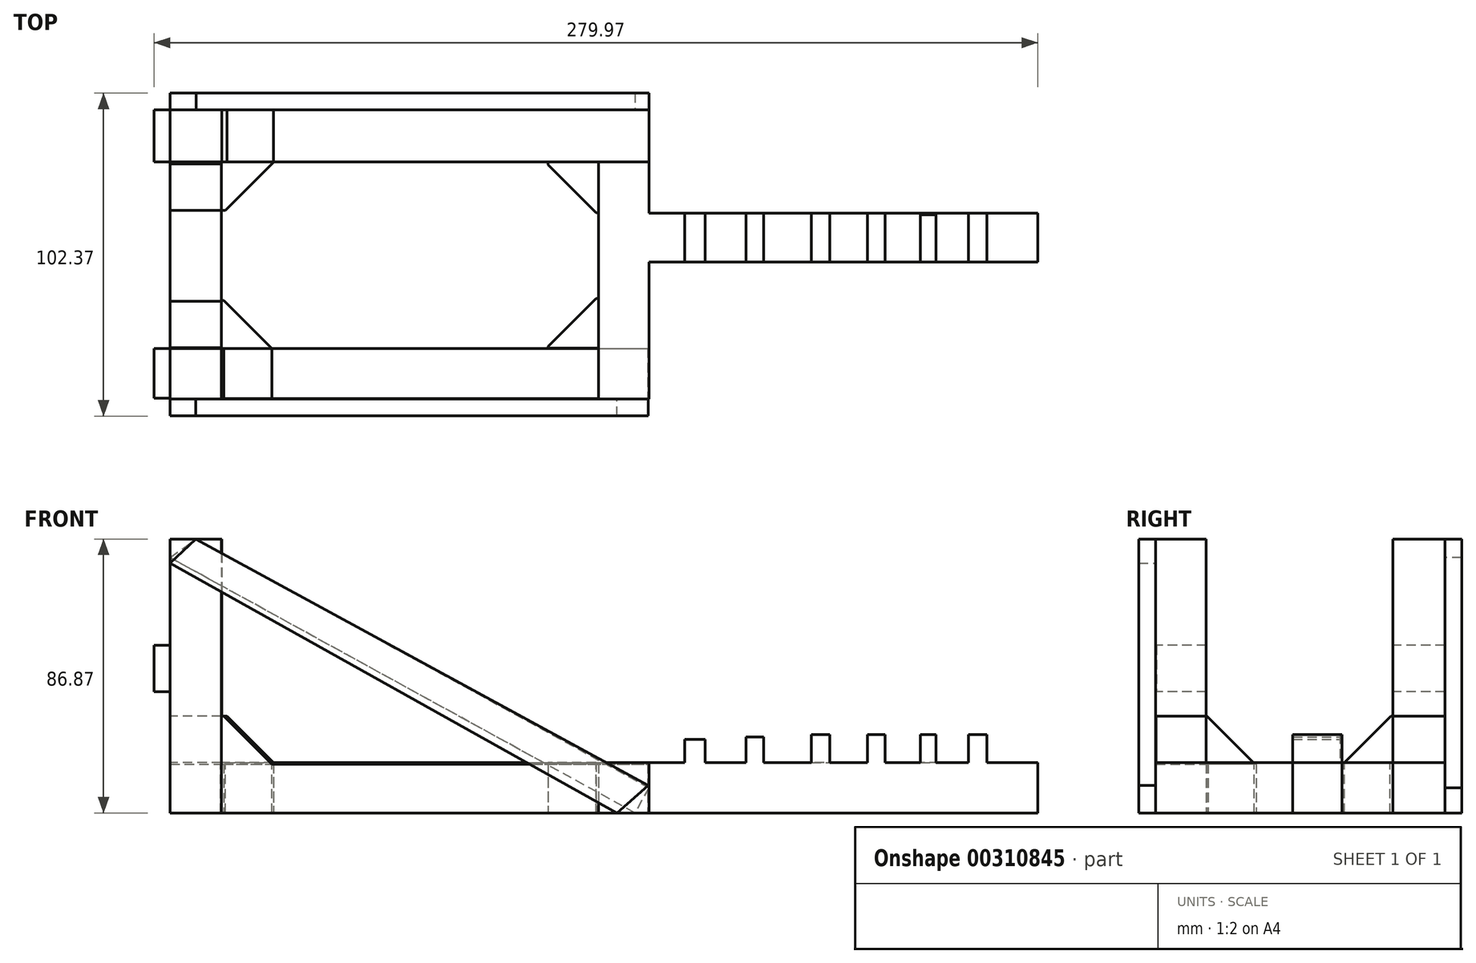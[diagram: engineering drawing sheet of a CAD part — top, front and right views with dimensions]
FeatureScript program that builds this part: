
annotation { "Feature Type Name" : "Feature", "Feature Type Description" : "" }
export const myFeature = defineFeature(function(context is Context, id is Id, definition is map)
    precondition{}
    {
        {
            var Q0;
            Q0=qCreatedBy(makeId("Top.planeOp"),FACE);
            var sketch = newSketch(context, id + "F0", { "sketchPlane" : qUnion([Q0])});
            skLineSegment(sketch, "E0.bottom", {"start": v(-76.1, 76.76) * mm, "end": v(75.59, 76.76) * mm});
            skLineSegment(sketch, "E0.top", {"start": v(-76.1, -76.47) * mm, "end": v(75.59, -76.47) * mm});
            skLineSegment(sketch, "E0.left", {"start": v(-76.1, 76.76) * mm, "end": v(-76.1, -76.47) * mm});
            skLineSegment(sketch, "E0.right", {"start": v(75.59, 76.76) * mm, "end": v(75.59, -76.47) * mm});
            skSolve(sketch);
        }
        {
            var Q0;
            Q0=makeQuery(id+"F0.imprint","IMPRINT",FACE,{"disambiguationData":[TD([[makeQuery(id+"F0.imprint","IMPRINT",EDGE,{"derivedFrom":sQuery(id+"F0.wireOp",EDGE,"E0.bottom")}),-1.0]])]});
            var sketch = newSketch(context, id + "F1", { "sketchPlane" : qUnion([Q0])});
            skLineSegment(sketch, "E1.bottom", {"start": v(-76.15, -35.2) * mm, "end": v(75.3, -35.2) * mm});
            skLineSegment(sketch, "E1.top", {"start": v(-76.15, -51.18) * mm, "end": v(75.3, -51.18) * mm});
            skLineSegment(sketch, "E1.left", {"start": v(-76.15, -35.2) * mm, "end": v(-76.15, -51.18) * mm});
            skLineSegment(sketch, "E1.right", {"start": v(75.3, -35.2) * mm, "end": v(75.3, -51.18) * mm});
            skSolve(sketch);
        }
        {
            var Q0;
            {var subQ0=sQuery(id+"F1.wireOp",EDGE,"E1.right");Q0=makeQuery(id+"F1.imprint","IMPRINT",FACE,{"disambiguationData":[TD([[makeQuery(id+"F1.imprint","IMPRINT",EDGE,{"derivedFrom":subQ0}),-1.0]])]});}
            extrude(context, id + "F2", {"entities" : qUnion([Q0]), "depth" : 15.5 * mm});
        }
        {
            var Q0;
            Q0=makeQuery(id+"F0.imprint","IMPRINT",FACE,{"disambiguationData":[TD([[makeQuery(id+"F0.imprint","IMPRINT",EDGE,{"derivedFrom":sQuery(id+"F0.wireOp",EDGE,"E0.bottom")}),-1.0]])]});
            var sketch = newSketch(context, id + "F3", { "sketchPlane" : qUnion([Q0])});
            skLineSegment(sketch, "E2.bottom", {"start": v(-76.62, 40.39) * mm, "end": v(75.96, 40.39) * mm});
            skLineSegment(sketch, "E2.top", {"start": v(-76.62, 23.87) * mm, "end": v(75.96, 23.87) * mm});
            skLineSegment(sketch, "E2.left", {"start": v(-76.62, 40.39) * mm, "end": v(-76.62, 23.87) * mm});
            skLineSegment(sketch, "E2.right", {"start": v(75.96, 40.39) * mm, "end": v(75.96, 23.87) * mm});
            skSolve(sketch);
        }
        {
            var Q0;
            {var subQ0=sQuery(id+"F3.wireOp",EDGE,"E2.bottom");var subQ1=makeQuery(id+"F0.imprint","IMPRINT",EDGE,{"derivedFrom":sQuery(id+"F0.wireOp",EDGE,"E0.left")});var subQ2=makeQuery(id+"F3.imprint","INTERSECT",VERTEX,{"derivedFrom":[subQ1,subQ0]});Q0=makeQuery(id+"F3.imprint","IMPRINT",FACE,{"disambiguationData":[TD([[makeQuery(id+"F3.imprint","IMPRINT",EDGE,{"disambiguationData":[TD([[subQ2,-1.0]])],"derivedFrom":subQ0}),-1.0]])]});}
            extrude(context, id + "F4", {"entities" : qUnion([Q0]), "depth" : 16 * mm});
        }
        {
            var Q0;
            Q0=makeQuery(id+"F4.opExtrude","SWEPT_FACE",FACE,{"disambiguationData":[OSD([sQuery(id+"F3.wireOp",EDGE,"E2.top")])]});
            var sketch = newSketch(context, id + "F5", { "sketchPlane" : qUnion([Q0])});
            skLineSegment(sketch, "E3.bottom", {"start": v(-76.1, 16) * mm, "end": v(-59.88, 16) * mm});
            skLineSegment(sketch, "E3.top", {"start": v(-76.1, 0) * mm, "end": v(-59.88, 0) * mm});
            skLineSegment(sketch, "E3.left", {"start": v(-76.1, 16) * mm, "end": v(-76.1, 0) * mm});
            skLineSegment(sketch, "E3.right", {"start": v(-59.88, 16) * mm, "end": v(-59.88, 0) * mm});
            skSolve(sketch);
        }
        {
            var Q0;
            Q0=makeQuery(id+"F5.imprint","IMPRINT",FACE,{"disambiguationData":[TD([[makeQuery(id+"F5.imprint","IMPRINT",EDGE,{"derivedFrom":sQuery(id+"F5.wireOp",EDGE,"E3.bottom")}),-1.0]])]});
            extrude(context, id + "F6", {"entities" : qUnion([Q0]), "depth" : 75.18 * mm});
        }
        {
            var Q0;
            Q0=makeQuery(id+"F4.opExtrude","SWEPT_FACE",FACE,{"disambiguationData":[OSD([sQuery(id+"F3.wireOp",EDGE,"E2.top")])]});
            var sketch = newSketch(context, id + "F7", { "sketchPlane" : qUnion([Q0])});
            skLineSegment(sketch, "E4.bottom", {"start": v(75.59, 16) * mm, "end": v(59.56, 16) * mm});
            skLineSegment(sketch, "E4.top", {"start": v(75.59, 0) * mm, "end": v(59.56, 0) * mm});
            skLineSegment(sketch, "E4.left", {"start": v(75.59, 16) * mm, "end": v(75.59, 0) * mm});
            skLineSegment(sketch, "E4.right", {"start": v(59.56, 16) * mm, "end": v(59.56, 0) * mm});
            skSolve(sketch);
        }
        {
            var Q0;
            Q0=makeQuery(id+"F7.imprint","IMPRINT",FACE,{"disambiguationData":[TD([[makeQuery(id+"F7.imprint","IMPRINT",EDGE,{"derivedFrom":sQuery(id+"F7.wireOp",EDGE,"E4.bottom")}),-1.0]])]});
            extrude(context, id + "F8", {"entities" : qUnion([Q0]), "depth" : 75.18 * mm});
        }
        {
            var Q0;
            Q0=makeQuery(id+"F4.opExtrude","CAP_FACE",FACE,{"disambiguationData":[OSD([sQuery(id+"F0.wireOp",EDGE,"E0.left"),sQuery(id+"F0.wireOp",EDGE,"E0.right"),sQuery(id+"F3.wireOp",EDGE,"E2.bottom"),sQuery(id+"F3.wireOp",EDGE,"E2.top")])],"isStart":false});
            var sketch = newSketch(context, id + "F9", { "sketchPlane" : qUnion([Q0])});
            skLineSegment(sketch, "E5.bottom", {"start": v(-76.1, 23.87) * mm, "end": v(-59.76, 23.87) * mm});
            skLineSegment(sketch, "E5.top", {"start": v(-76.1, 40.39) * mm, "end": v(-59.76, 40.39) * mm});
            skLineSegment(sketch, "E5.left", {"start": v(-76.1, 23.87) * mm, "end": v(-76.1, 40.39) * mm});
            skLineSegment(sketch, "E5.right", {"start": v(-59.76, 23.87) * mm, "end": v(-59.76, 40.39) * mm});
            skSolve(sketch);
        }
        {
            var Q0;
            Q0=makeQuery(id+"F9.imprint","IMPRINT",FACE,{"disambiguationData":[TD([[makeQuery(id+"F9.imprint","IMPRINT",EDGE,{"derivedFrom":sQuery(id+"F9.wireOp",EDGE,"E5.bottom")}),1.0]])]});
            extrude(context, id + "F10", {"entities" : qUnion([Q0]), "operationType" : NewBodyOperationType.ADD, "depth" : 70.87 * mm});
        }
        {
            var Q0;
            Q0=makeQuery(id+"F6.opExtrude","SWEPT_FACE",FACE,{"disambiguationData":[OSD([sQuery(id+"F5.wireOp",EDGE,"E3.bottom")])]});
            var sketch = newSketch(context, id + "F11", { "sketchPlane" : qUnion([Q0])});
            skLineSegment(sketch, "E6.bottom", {"start": v(-59.88, -35.24) * mm, "end": v(-76.1, -35.24) * mm});
            skLineSegment(sketch, "E6.top", {"start": v(-59.88, -51.31) * mm, "end": v(-76.1, -51.31) * mm});
            skLineSegment(sketch, "E6.left", {"start": v(-59.88, -35.24) * mm, "end": v(-59.88, -51.31) * mm});
            skLineSegment(sketch, "E6.right", {"start": v(-76.1, -35.24) * mm, "end": v(-76.1, -51.31) * mm});
            skSolve(sketch);
        }
        {
            var Q0;
            Q0=makeQuery(id+"F11.imprint","IMPRINT",FACE,{"disambiguationData":[TD([[makeQuery(id+"F11.imprint","IMPRINT",EDGE,{"derivedFrom":sQuery(id+"F11.wireOp",EDGE,"E6.bottom")}),1.0]])]});
            extrude(context, id + "F12", {"entities" : qUnion([Q0]), "operationType" : NewBodyOperationType.ADD, "depth" : 70.87 * mm});
        }
        {
            var Q0;
            Q0=makeQuery(id+"F10.boolean.opBoolean","MERGE",FACE,{"derivedFrom":[makeQuery(id+"F4.opExtrude","SWEPT_FACE",FACE,{"disambiguationData":[OSD([sQuery(id+"F3.wireOp",EDGE,"E2.bottom")])]}),makeQuery(id+"F10.opExtrude","SWEPT_FACE",FACE,{"disambiguationData":[OSD([sQuery(id+"F9.wireOp",EDGE,"E5.top")])]})]});
            var sketch = newSketch(context, id + "F13", { "sketchPlane" : qUnion([Q0])});
            skLineSegment(sketch, "E7", {"start": v(67.93, 86.87) * mm, "end": v(-75.59, 8) * mm});
            skLineSegment(sketch, "E8", {"start": v(-75.59, 8) * mm, "end": v(-71.19, 0) * mm});
            skLineSegment(sketch, "E9", {"start": v(-71.19, 0) * mm, "end": v(76.1, 80.94) * mm});
            skLineSegment(sketch, "E10", {"start": v(76.1, 80.94) * mm, "end": v(67.93, 86.87) * mm});
            skSolve(sketch);
        }
        {
            var Q0;
            {var subQ0=sQuery(id+"F13.wireOp",EDGE,"E7");var subQ1=sQuery(id+"F3.wireOp",EDGE,"E2.bottom");var subQ4=makeQuery(id+"F4.opExtrude","CAP_EDGE",EDGE,{"disambiguationData":[OSD([subQ1])],"isStart":false});var subQ5=makeQuery(id+"F13.imprint","INTERSECT",VERTEX,{"derivedFrom":[subQ4,subQ0]});Q0=makeQuery(id+"F13.imprint","IMPRINT",FACE,{"disambiguationData":[TD([[makeQuery(id+"F13.imprint","IMPRINT",EDGE,{"disambiguationData":[TD([[subQ5,1.0]])],"derivedFrom":subQ4}),-1.0]])]});}
            var Q1;
            {var subQ0=sQuery(id+"F13.wireOp",EDGE,"E10");Q1=makeQuery(id+"F13.imprint","IMPRINT",FACE,{"disambiguationData":[TD([[makeQuery(id+"F13.imprint","IMPRINT",EDGE,{"derivedFrom":subQ0}),1.0]])]});}
            var Q2;
            {var subQ0=sQuery(id+"F13.wireOp",EDGE,"E8");Q2=makeQuery(id+"F13.imprint","IMPRINT",FACE,{"disambiguationData":[TD([[makeQuery(id+"F13.imprint","IMPRINT",EDGE,{"derivedFrom":subQ0}),1.0]])]});}
            extrude(context, id + "F14", {"entities" : qUnion([Q0, Q1, Q2]), "operationType" : NewBodyOperationType.ADD, "depth" : 5.33 * mm});
        }
        {
            var Q0;
            Q0=makeQuery(id+"F12.boolean.opBoolean","MERGE",FACE,{"derivedFrom":[makeQuery(id+"F6.opExtrude","CAP_FACE",FACE,{"disambiguationData":[OSD([sQuery(id+"F5.wireOp",EDGE,"E3.bottom"),sQuery(id+"F5.wireOp",EDGE,"E3.top"),sQuery(id+"F5.wireOp",EDGE,"E3.left"),sQuery(id+"F5.wireOp",EDGE,"E3.right")])],"isStart":false}),makeQuery(id+"F12.opExtrude","SWEPT_FACE",FACE,{"disambiguationData":[OSD([sQuery(id+"F11.wireOp",EDGE,"E6.top")])]})]});
            var sketch = newSketch(context, id + "F15", { "sketchPlane" : qUnion([Q0])});
            skLineSegment(sketch, "E11", {"start": v(-68, 86.87) * mm, "end": v(75.37, 8.72) * mm});
            skLineSegment(sketch, "E12", {"start": v(75.37, 8.72) * mm, "end": v(65.52, 0) * mm});
            skLineSegment(sketch, "E13", {"start": v(65.52, 0) * mm, "end": v(-76.1, 79.26) * mm});
            skLineSegment(sketch, "E14", {"start": v(-76.1, 79.26) * mm, "end": v(-68, 86.87) * mm});
            skSolve(sketch);
        }
        {
            var Q0;
            {var subQ0=sQuery(id+"F15.wireOp",EDGE,"E12");Q0=makeQuery(id+"F15.imprint","IMPRINT",FACE,{"disambiguationData":[TD([[makeQuery(id+"F15.imprint","IMPRINT",EDGE,{"derivedFrom":subQ0}),-1.0]])]});}
            var Q1;
            {var subQ0=sQuery(id+"F15.wireOp",EDGE,"E14");Q1=makeQuery(id+"F15.imprint","IMPRINT",FACE,{"disambiguationData":[TD([[makeQuery(id+"F15.imprint","IMPRINT",EDGE,{"derivedFrom":subQ0}),-1.0]])]});}
            extrude(context, id + "F16", {"entities" : qUnion([Q0, Q1]), "depth" : 5.33 * mm});
        }
        {
            var Q0;
            Q0=makeQuery(id+"F4.opExtrude","CAP_FACE",FACE,{"disambiguationData":[OSD([sQuery(id+"F0.wireOp",EDGE,"E0.left"),sQuery(id+"F0.wireOp",EDGE,"E0.right"),sQuery(id+"F3.wireOp",EDGE,"E2.bottom"),sQuery(id+"F3.wireOp",EDGE,"E2.top")])],"isStart":false});
            var sketch = newSketch(context, id + "F17", { "sketchPlane" : qUnion([Q0])});
            skLineSegment(sketch, "E15", {"start": v(-59.76, 40.39) * mm, "end": v(-59.76, 23.87) * mm});
            skLineSegment(sketch, "E16", {"start": v(-59.76, 23.87) * mm, "end": v(-42.9, 23.87) * mm});
            skLineSegment(sketch, "E17", {"start": v(-42.9, 23.87) * mm, "end": v(-42.9, 40.39) * mm});
            skLineSegment(sketch, "E18", {"start": v(-42.9, 40.39) * mm, "end": v(-59.76, 40.39) * mm});
            skLineSegment(sketch, "E19", {"start": v(-59.76, 23.87) * mm, "end": v(-59.76, 40.39) * mm});
            skLineSegment(sketch, "E20", {"start": v(-42.9, 23.87) * mm, "end": v(-59.76, 23.87) * mm});
            skLineSegment(sketch, "E21", {"start": v(-59.76, 40.39) * mm, "end": v(-42.9, 40.39) * mm});
            skSolve(sketch);
        }
        {
            var Q0;
            Q0=makeQuery(id+"F17.imprint","IMPRINT",FACE,{"disambiguationData":[TD([[makeQuery(id+"F17.imprint","IMPRINT",EDGE,{"derivedFrom":sQuery(id+"F17.wireOp",EDGE,"E17")}),1.0]])]});
            extrude(context, id + "F18", {"entities" : qUnion([Q0]), "operationType" : NewBodyOperationType.ADD, "depth" : 14.73 * mm});
        }
        {
            var Q0;
            Q0=makeQuery(id+"F10.boolean.opBoolean","MERGE",FACE,{"derivedFrom":[makeQuery(id+"F4.opExtrude","SWEPT_FACE",FACE,{"disambiguationData":[OSD([sQuery(id+"F0.wireOp",EDGE,"E0.left")])]}),makeQuery(id+"F10.opExtrude","SWEPT_FACE",FACE,{"disambiguationData":[OSD([sQuery(id+"F9.wireOp",EDGE,"E5.left")])]})]});
            var sketch = newSketch(context, id + "F19", { "sketchPlane" : qUnion([Q0])});
            skLineSegment(sketch, "E22.bottom", {"start": v(-40.39, 53.11) * mm, "end": v(51.06, 53.11) * mm});
            skLineSegment(sketch, "E22.top", {"start": v(-40.39, 38.44) * mm, "end": v(51.06, 38.44) * mm});
            skLineSegment(sketch, "E22.left", {"start": v(-40.39, 53.11) * mm, "end": v(-40.39, 38.44) * mm});
            skLineSegment(sketch, "E22.right", {"start": v(51.06, 53.11) * mm, "end": v(51.06, 38.44) * mm});
            skSolve(sketch);
        }
        {
            var Q0;
            {var subQ0=sQuery(id+"F19.wireOp",EDGE,"E22.right");Q0=makeQuery(id+"F19.imprint","IMPRINT",FACE,{"disambiguationData":[TD([[makeQuery(id+"F19.imprint","IMPRINT",EDGE,{"derivedFrom":subQ0}),-1.0]])]});}
            var Q1;
            {var subQ0=sQuery(id+"F19.wireOp",EDGE,"E22.left");Q1=makeQuery(id+"F19.imprint","IMPRINT",FACE,{"disambiguationData":[TD([[makeQuery(id+"F19.imprint","IMPRINT",EDGE,{"derivedFrom":subQ0}),1.0]])]});}
            extrude(context, id + "F20", {"entities" : qUnion([Q0, Q1]), "depth" : 5.08 * mm});
        }
        {
            var Q0;
            Q0=makeQuery(id+"F8.opExtrude","SWEPT_FACE",FACE,{"disambiguationData":[OSD([sQuery(id+"F7.wireOp",EDGE,"E4.left")])]});
            var sketch = newSketch(context, id + "F21", { "sketchPlane" : qUnion([Q0])});
            skLineSegment(sketch, "E23.bottom", {"start": v(-7.8, 16) * mm, "end": v(7.73, 16) * mm});
            skLineSegment(sketch, "E23.top", {"start": v(-7.8, 0) * mm, "end": v(7.73, 0) * mm});
            skLineSegment(sketch, "E23.left", {"start": v(-7.8, 16) * mm, "end": v(-7.8, 0) * mm});
            skLineSegment(sketch, "E23.right", {"start": v(7.73, 16) * mm, "end": v(7.73, 0) * mm});
            skSolve(sketch);
        }
        {
            var Q0;
            Q0=makeQuery(id+"F21.imprint","IMPRINT",FACE,{"disambiguationData":[TD([[makeQuery(id+"F21.imprint","IMPRINT",EDGE,{"derivedFrom":sQuery(id+"F21.wireOp",EDGE,"E23.bottom")}),-1.0]])]});
            extrude(context, id + "F22", {"entities" : qUnion([Q0]), "operationType" : NewBodyOperationType.ADD, "depth" : 123.19 * mm});
        }
        {
            var Q0;
            Q0=makeQuery(id+"F22.boolean.opBoolean","MERGE",FACE,{"derivedFrom":[makeQuery(id+"F8.opExtrude","SWEPT_FACE",FACE,{"disambiguationData":[OSD([sQuery(id+"F7.wireOp",EDGE,"E4.bottom")])]}),makeQuery(id+"F22.opExtrude","SWEPT_FACE",FACE,{"disambiguationData":[OSD([sQuery(id+"F21.wireOp",EDGE,"E23.bottom")])]})]});
            var sketch = newSketch(context, id + "F23", { "sketchPlane" : qUnion([Q0])});
            skLineSegment(sketch, "E24.bottom", {"start": v(93.36, -7.8) * mm, "end": v(86.95, -7.8) * mm});
            skLineSegment(sketch, "E24.top", {"start": v(93.36, 7.73) * mm, "end": v(86.95, 7.73) * mm});
            skLineSegment(sketch, "E24.left", {"start": v(93.36, -7.8) * mm, "end": v(93.36, 7.73) * mm});
            skLineSegment(sketch, "E24.right", {"start": v(86.95, -7.8) * mm, "end": v(86.95, 7.73) * mm});
            skSolve(sketch);
        }
        {
            var Q0;
            Q0=makeQuery(id+"F23.imprint","IMPRINT",FACE,{"disambiguationData":[TD([[makeQuery(id+"F23.imprint","IMPRINT",EDGE,{"derivedFrom":sQuery(id+"F23.wireOp",EDGE,"E24.bottom")}),-1.0]])]});
            extrude(context, id + "F24", {"entities" : qUnion([Q0]), "operationType" : NewBodyOperationType.ADD, "depth" : 7.37 * mm});
        }
        {
            var Q0;
            {var subQ2=sQuery(id+"F21.wireOp",EDGE,"E23.bottom");Q0=makeQuery(id+"F24.boolean.opBoolean","SPLIT",FACE,{"disambiguationData":[TD([makeQuery(id+"F24.opExtrude","SWEPT_FACE",FACE,{"disambiguationData":[OSD([sQuery(id+"F23.wireOp",EDGE,"E24.left")])]})])],"derivedFrom":makeQuery(id+"F22.boolean.opBoolean","MERGE",FACE,{"derivedFrom":[makeQuery(id+"F8.opExtrude","SWEPT_FACE",FACE,{"disambiguationData":[OSD([sQuery(id+"F7.wireOp",EDGE,"E4.bottom")])]}),makeQuery(id+"F22.opExtrude","SWEPT_FACE",FACE,{"disambiguationData":[OSD([subQ2])]})]})});}
            var sketch = newSketch(context, id + "F25", { "sketchPlane" : qUnion([Q0])});
            skLineSegment(sketch, "E25.bottom", {"start": v(112, -7.8) * mm, "end": v(106.38, -7.8) * mm});
            skLineSegment(sketch, "E25.top", {"start": v(112, 7.73) * mm, "end": v(106.38, 7.73) * mm});
            skLineSegment(sketch, "E25.left", {"start": v(112, -7.8) * mm, "end": v(112, 7.73) * mm});
            skLineSegment(sketch, "E25.right", {"start": v(106.38, -7.8) * mm, "end": v(106.38, 7.73) * mm});
            skSolve(sketch);
        }
        {
            var Q0;
            {var subQ0=sQuery(id+"F25.wireOp",EDGE,"E25.left");Q0=makeQuery(id+"F25.imprint","IMPRINT",FACE,{"disambiguationData":[TD([[makeQuery(id+"F25.imprint","IMPRINT",EDGE,{"derivedFrom":subQ0}),-1.0]])]});}
            var sketch = newSketch(context, id + "F26", { "sketchPlane" : qUnion([Q0])});
            skLineSegment(sketch, "E26.bottom", {"start": v(127.05, 7.71) * mm, "end": v(132.9, 7.71) * mm});
            skLineSegment(sketch, "E26.top", {"start": v(127.05, -8.27) * mm, "end": v(132.9, -8.27) * mm});
            skLineSegment(sketch, "E26.left", {"start": v(127.05, 7.71) * mm, "end": v(127.05, -8.27) * mm});
            skLineSegment(sketch, "E26.right", {"start": v(132.9, 7.71) * mm, "end": v(132.9, -8.27) * mm});
            skSolve(sketch);
        }
        {
            var Q0;
            Q0=makeQuery(id+"F25.imprint","IMPRINT",FACE,{"disambiguationData":[TD([[makeQuery(id+"F25.imprint","IMPRINT",EDGE,{"derivedFrom":sQuery(id+"F25.wireOp",EDGE,"E25.bottom")}),-1.0]])]});
            extrude(context, id + "F27", {"entities" : qUnion([Q0]), "operationType" : NewBodyOperationType.ADD, "depth" : 8.13 * mm});
        }
        {
            var Q0;
            {var subQ0=sQuery(id+"F26.wireOp",EDGE,"E26.bottom");Q0=makeQuery(id+"F26.imprint","IMPRINT",FACE,{"disambiguationData":[TD([[makeQuery(id+"F26.imprint","IMPRINT",EDGE,{"derivedFrom":subQ0}),-1.0]])]});}
            extrude(context, id + "F28", {"entities" : qUnion([Q0]), "operationType" : NewBodyOperationType.ADD, "depth" : 8.9 * mm});
        }
        {
            var Q0;
            {var subQ5=sQuery(id+"F21.wireOp",EDGE,"E23.bottom");Q0=makeQuery(id+"F27.boolean.opBoolean","SPLIT",FACE,{"disambiguationData":[TD([makeQuery(id+"F27.opExtrude","SWEPT_FACE",FACE,{"disambiguationData":[OSD([sQuery(id+"F25.wireOp",EDGE,"E25.left")])]})])],"derivedFrom":makeQuery(id+"F24.boolean.opBoolean","SPLIT",FACE,{"disambiguationData":[TD([makeQuery(id+"F24.opExtrude","SWEPT_FACE",FACE,{"disambiguationData":[OSD([sQuery(id+"F23.wireOp",EDGE,"E24.left")])]})])],"derivedFrom":makeQuery(id+"F22.boolean.opBoolean","MERGE",FACE,{"derivedFrom":[makeQuery(id+"F8.opExtrude","SWEPT_FACE",FACE,{"disambiguationData":[OSD([sQuery(id+"F7.wireOp",EDGE,"E4.bottom")])]}),makeQuery(id+"F22.opExtrude","SWEPT_FACE",FACE,{"disambiguationData":[OSD([subQ5])]})]})})});}
            var sketch = newSketch(context, id + "F29", { "sketchPlane" : qUnion([Q0])});
            skLineSegment(sketch, "E27.bottom", {"start": v(144.87, 7.73) * mm, "end": v(150.46, 7.73) * mm});
            skLineSegment(sketch, "E27.top", {"start": v(144.87, -7.8) * mm, "end": v(150.46, -7.8) * mm});
            skLineSegment(sketch, "E27.left", {"start": v(144.87, 7.73) * mm, "end": v(144.87, -7.8) * mm});
            skLineSegment(sketch, "E27.right", {"start": v(150.46, 7.73) * mm, "end": v(150.46, -7.8) * mm});
            skSolve(sketch);
        }
        {
            var Q0;
            {var subQ0=sQuery(id+"F29.wireOp",EDGE,"E27.right");Q0=makeQuery(id+"F29.imprint","IMPRINT",FACE,{"disambiguationData":[TD([[makeQuery(id+"F29.imprint","IMPRINT",EDGE,{"derivedFrom":subQ0}),1.0]])]});}
            var sketch = newSketch(context, id + "F30", { "sketchPlane" : qUnion([Q0])});
            skLineSegment(sketch, "E28.bottom", {"start": v(161.65, 7.14) * mm, "end": v(166.62, 7.14) * mm});
            skLineSegment(sketch, "E28.top", {"start": v(161.65, -8.09) * mm, "end": v(166.62, -8.09) * mm});
            skLineSegment(sketch, "E28.left", {"start": v(161.65, 7.14) * mm, "end": v(161.65, -8.09) * mm});
            skLineSegment(sketch, "E28.right", {"start": v(166.62, 7.14) * mm, "end": v(166.62, -8.09) * mm});
            skSolve(sketch);
        }
        {
            var Q0;
            Q0=makeQuery(id+"F29.imprint","IMPRINT",FACE,{"disambiguationData":[TD([[makeQuery(id+"F29.imprint","IMPRINT",EDGE,{"derivedFrom":sQuery(id+"F29.wireOp",EDGE,"E27.bottom")}),1.0]])]});
            extrude(context, id + "F31", {"entities" : qUnion([Q0]), "operationType" : NewBodyOperationType.ADD, "depth" : 8.9 * mm});
        }
        {
            var Q0;
            {var subQ0=sQuery(id+"F30.wireOp",EDGE,"E28.bottom");Q0=makeQuery(id+"F30.imprint","IMPRINT",FACE,{"disambiguationData":[TD([[makeQuery(id+"F30.imprint","IMPRINT",EDGE,{"derivedFrom":subQ0}),-1.0]])]});}
            extrude(context, id + "F32", {"entities" : qUnion([Q0]), "operationType" : NewBodyOperationType.ADD, "depth" : 8.9 * mm});
        }
        {
            var Q0;
            {var subQ3=sQuery(id+"F21.wireOp",EDGE,"E23.bottom");var subQ4=sQuery(id+"F7.wireOp",EDGE,"E4.bottom");Q0=makeQuery(id+"F31.boolean.opBoolean","SPLIT",FACE,{"disambiguationData":[TD([makeQuery(id+"F31.opExtrude","SWEPT_FACE",FACE,{"disambiguationData":[OSD([sQuery(id+"F29.wireOp",EDGE,"E27.right")])]})])],"derivedFrom":makeQuery(id+"F27.boolean.opBoolean","SPLIT",FACE,{"disambiguationData":[TD([makeQuery(id+"F27.opExtrude","SWEPT_FACE",FACE,{"disambiguationData":[OSD([sQuery(id+"F25.wireOp",EDGE,"E25.left")])]})])],"derivedFrom":makeQuery(id+"F24.boolean.opBoolean","SPLIT",FACE,{"disambiguationData":[TD([makeQuery(id+"F24.opExtrude","SWEPT_FACE",FACE,{"disambiguationData":[OSD([sQuery(id+"F23.wireOp",EDGE,"E24.left")])]})])],"derivedFrom":makeQuery(id+"F22.boolean.opBoolean","MERGE",FACE,{"derivedFrom":[makeQuery(id+"F8.opExtrude","SWEPT_FACE",FACE,{"disambiguationData":[OSD([subQ4])]}),makeQuery(id+"F22.opExtrude","SWEPT_FACE",FACE,{"disambiguationData":[OSD([subQ3])]})]})})})});}
            var sketch = newSketch(context, id + "F33", { "sketchPlane" : qUnion([Q0])});
            skLineSegment(sketch, "E29.bottom", {"start": v(176.78, 7.73) * mm, "end": v(182.7, 7.73) * mm});
            skLineSegment(sketch, "E29.top", {"start": v(176.78, -7.8) * mm, "end": v(182.7, -7.8) * mm});
            skLineSegment(sketch, "E29.left", {"start": v(176.78, 7.73) * mm, "end": v(176.78, -7.8) * mm});
            skLineSegment(sketch, "E29.right", {"start": v(182.7, 7.73) * mm, "end": v(182.7, -7.8) * mm});
            skSolve(sketch);
        }
        {
            var Q0;
            Q0=makeQuery(id+"F33.imprint","IMPRINT",FACE,{"disambiguationData":[TD([[makeQuery(id+"F33.imprint","IMPRINT",EDGE,{"derivedFrom":sQuery(id+"F33.wireOp",EDGE,"E29.bottom")}),1.0]])]});
            extrude(context, id + "F34", {"entities" : qUnion([Q0]), "operationType" : NewBodyOperationType.ADD, "depth" : 8.9 * mm});
        }
        {
            var Q0;
            Q0=makeQuery(id+"F2.opExtrude","CAP_FACE",FACE,{"disambiguationData":[OSD([sQuery(id+"F0.wireOp",EDGE,"E0.left"),sQuery(id+"F1.wireOp",EDGE,"E1.bottom"),sQuery(id+"F1.wireOp",EDGE,"E1.top"),sQuery(id+"F1.wireOp",EDGE,"E1.right")])],"isStart":false});
            var sketch = newSketch(context, id + "F35", { "sketchPlane" : qUnion([Q0])});
            skLineSegment(sketch, "E30.bottom", {"start": v(-59.83, -51.18) * mm, "end": v(-43.85, -51.18) * mm});
            skLineSegment(sketch, "E30.top", {"start": v(-59.83, -35.2) * mm, "end": v(-43.85, -35.2) * mm});
            skLineSegment(sketch, "E30.left", {"start": v(-59.83, -51.18) * mm, "end": v(-59.83, -35.2) * mm});
            skLineSegment(sketch, "E30.right", {"start": v(-43.85, -51.18) * mm, "end": v(-43.85, -35.2) * mm});
            skSolve(sketch);
        }
        {
            var Q0;
            Q0=makeQuery(id+"F35.imprint","IMPRINT",FACE,{"disambiguationData":[TD([[makeQuery(id+"F35.imprint","IMPRINT",EDGE,{"derivedFrom":sQuery(id+"F35.wireOp",EDGE,"E30.bottom")}),1.0]])]});
            extrude(context, id + "F36", {"entities" : qUnion([Q0]), "operationType" : NewBodyOperationType.ADD, "depth" : 15.24 * mm});
        }
        {
            var Q0;
            Q0=makeQuery(id+"F36.opExtrude","CAP_EDGE",EDGE,{"disambiguationData":[OSD([sQuery(id+"F35.wireOp",EDGE,"E30.right")])],"isStart":false});
            chamfer(context, id + "F37", {"entities" : qUnion([Q0]), "width" : 15.24 * mm, "tangentPropagation" : true});
        }
        {
            var Q0;
            Q0=makeQuery(id+"F18.opExtrude","CAP_EDGE",EDGE,{"disambiguationData":[OSD([sQuery(id+"F17.wireOp",EDGE,"E17")])],"isStart":false});
            chamfer(context, id + "F38", {"entities" : qUnion([Q0]), "width" : 15.24 * mm, "tangentPropagation" : true});
        }
        {
            var Q0;
            Q0=makeQuery(id+"F6.opExtrude","SWEPT_FACE",FACE,{"disambiguationData":[OSD([sQuery(id+"F5.wireOp",EDGE,"E3.bottom")])]});
            var sketch = newSketch(context, id + "F39", { "sketchPlane" : qUnion([Q0])});
            skLineSegment(sketch, "E31.bottom", {"start": v(-76.1, -35.24) * mm, "end": v(-59.88, -35.24) * mm});
            skLineSegment(sketch, "E31.top", {"start": v(-76.1, -19.8) * mm, "end": v(-59.88, -19.8) * mm});
            skLineSegment(sketch, "E31.left", {"start": v(-76.1, -35.24) * mm, "end": v(-76.1, -19.8) * mm});
            skLineSegment(sketch, "E31.right", {"start": v(-59.88, -35.24) * mm, "end": v(-59.88, -19.8) * mm});
            skLineSegment(sketch, "E32.left", {"start": v(-76.1, -19.8) * mm, "end": v(-76.1, -19.8) * mm});
            skLineSegment(sketch, "E32.right", {"start": v(-59.88, -19.8) * mm, "end": v(-59.88, -19.8) * mm});
            skSolve(sketch);
        }
        {
            var Q0;
            Q0=makeQuery(id+"F39.imprint","IMPRINT",FACE,{"disambiguationData":[TD([[makeQuery(id+"F39.imprint","IMPRINT",EDGE,{"derivedFrom":sQuery(id+"F39.wireOp",EDGE,"E31.bottom")}),-1.0]])]});
            extrude(context, id + "F40", {"entities" : qUnion([Q0]), "operationType" : NewBodyOperationType.ADD, "depth" : 14.73 * mm});
        }
        {
            var Q0;
            Q0=makeQuery(id+"F40.opExtrude","CAP_EDGE",EDGE,{"disambiguationData":[OSD([sQuery(id+"F39.wireOp",EDGE,"E31.top")])],"isStart":false});
            chamfer(context, id + "F41", {"entities" : qUnion([Q0]), "width" : 15.24 * mm, "tangentPropagation" : true});
        }
        {
            var Q0;
            Q0=makeQuery(id+"F36.boolean.opBoolean","MERGE",FACE,{"derivedFrom":[makeQuery(id+"F2.opExtrude","SWEPT_FACE",FACE,{"disambiguationData":[OSD([sQuery(id+"F1.wireOp",EDGE,"E1.bottom")])]}),makeQuery(id+"F36.opExtrude","SWEPT_FACE",FACE,{"disambiguationData":[OSD([sQuery(id+"F35.wireOp",EDGE,"E30.top")])]})]});
            var sketch = newSketch(context, id + "F42", { "sketchPlane" : qUnion([Q0])});
            skLineSegment(sketch, "E33.bottom", {"start": v(60.1, 0) * mm, "end": v(43.85, 0) * mm});
            skLineSegment(sketch, "E33.top", {"start": v(60.1, 15.5) * mm, "end": v(43.85, 15.5) * mm});
            skLineSegment(sketch, "E33.left", {"start": v(60.1, 0) * mm, "end": v(60.1, 15.5) * mm});
            skLineSegment(sketch, "E33.right", {"start": v(43.85, 0) * mm, "end": v(43.85, 15.5) * mm});
            skSolve(sketch);
        }
        {
            var Q0;
            Q0=makeQuery(id+"F42.imprint","IMPRINT",FACE,{"disambiguationData":[TD([[makeQuery(id+"F42.imprint","IMPRINT",EDGE,{"derivedFrom":sQuery(id+"F42.wireOp",EDGE,"E33.bottom")}),-1.0]])]});
            extrude(context, id + "F43", {"entities" : qUnion([Q0]), "depth" : 15.24 * mm});
        }
        {
            var Q0;
            Q0=makeQuery(id+"F43.opExtrude","CAP_EDGE",EDGE,{"disambiguationData":[OSD([sQuery(id+"F42.wireOp",EDGE,"E33.right")])],"isStart":false});
            chamfer(context, id + "F44", {"entities" : qUnion([Q0]), "width" : 15.24 * mm, "tangentPropagation" : true});
        }
        {
            var Q0;
            Q0=makeQuery(id+"F6.opExtrude","SWEPT_FACE",FACE,{"disambiguationData":[OSD([sQuery(id+"F5.wireOp",EDGE,"E3.bottom")])]});
            var sketch = newSketch(context, id + "F45", { "sketchPlane" : qUnion([Q0])});
            skLineSegment(sketch, "E34.bottom", {"start": v(-76.1, 23.87) * mm, "end": v(-59.88, 23.87) * mm});
            skLineSegment(sketch, "E34.top", {"start": v(-76.1, 8.02) * mm, "end": v(-59.88, 8.02) * mm});
            skLineSegment(sketch, "E34.left", {"start": v(-76.1, 23.87) * mm, "end": v(-76.1, 8.02) * mm});
            skLineSegment(sketch, "E34.right", {"start": v(-59.88, 23.87) * mm, "end": v(-59.88, 8.02) * mm});
            skSolve(sketch);
        }
        {
            var Q0;
            Q0=makeQuery(id+"F45.imprint","IMPRINT",FACE,{"disambiguationData":[TD([[makeQuery(id+"F45.imprint","IMPRINT",EDGE,{"derivedFrom":sQuery(id+"F45.wireOp",EDGE,"E34.bottom")}),-1.0]])]});
            extrude(context, id + "F46", {"entities" : qUnion([Q0]), "depth" : 14.73 * mm});
        }
        {
            var Q0;
            Q0=makeQuery(id+"F46.opExtrude","CAP_EDGE",EDGE,{"disambiguationData":[OSD([sQuery(id+"F45.wireOp",EDGE,"E34.top")])],"isStart":false});
            chamfer(context, id + "F47", {"entities" : qUnion([Q0]), "width" : 15.24 * mm, "tangentPropagation" : true});
        }
        {
            var Q0;
            Q0=makeQuery(id+"F40.boolean.opBoolean","MERGE",FACE,{"derivedFrom":[makeQuery(id+"F12.boolean.opBoolean","MERGE",FACE,{"derivedFrom":[makeQuery(id+"F6.opExtrude","SWEPT_FACE",FACE,{"disambiguationData":[OSD([sQuery(id+"F5.wireOp",EDGE,"E3.right")])]}),makeQuery(id+"F12.opExtrude","SWEPT_FACE",FACE,{"disambiguationData":[OSD([sQuery(id+"F11.wireOp",EDGE,"E6.left")])]})]}),makeQuery(id+"F40.opExtrude","SWEPT_FACE",FACE,{"disambiguationData":[OSD([sQuery(id+"F39.wireOp",EDGE,"E31.right")])]})]});
            var sketch = newSketch(context, id + "F48", { "sketchPlane" : qUnion([Q0])});
            skLineSegment(sketch, "E35.bottom", {"start": v(8.56, 16) * mm, "end": v(23.87, 16) * mm});
            skLineSegment(sketch, "E35.top", {"start": v(8.56, 0) * mm, "end": v(23.87, 0) * mm});
            skLineSegment(sketch, "E35.left", {"start": v(8.56, 16) * mm, "end": v(8.56, 0) * mm});
            skLineSegment(sketch, "E35.right", {"start": v(23.87, 16) * mm, "end": v(23.87, 0) * mm});
            skSolve(sketch);
        }
        {
            var Q0;
            Q0=makeQuery(id+"F48.imprint","IMPRINT",FACE,{"disambiguationData":[TD([[makeQuery(id+"F48.imprint","IMPRINT",EDGE,{"derivedFrom":sQuery(id+"F48.wireOp",EDGE,"E35.bottom")}),-1.0]])]});
            extrude(context, id + "F49", {"entities" : qUnion([Q0]), "depth" : 16.5 * mm});
        }
        {
            var Q0;
            Q0=makeQuery(id+"F49.opExtrude","CAP_EDGE",EDGE,{"disambiguationData":[OSD([sQuery(id+"F48.wireOp",EDGE,"E35.left")])],"isStart":false});
            chamfer(context, id + "F50", {"entities" : qUnion([Q0]), "width" : 15.24 * mm, "tangentPropagation" : true});
        }
        {
            var Q0;
            Q0=makeQuery(id+"F8.opExtrude","SWEPT_FACE",FACE,{"disambiguationData":[OSD([sQuery(id+"F7.wireOp",EDGE,"E4.right")])]});
            var sketch = newSketch(context, id + "F51", { "sketchPlane" : qUnion([Q0])});
            skLineSegment(sketch, "E36.bottom", {"start": v(-23.87, 16) * mm, "end": v(-7.82, 16) * mm});
            skLineSegment(sketch, "E36.top", {"start": v(-23.87, 0) * mm, "end": v(-7.82, 0) * mm});
            skLineSegment(sketch, "E36.left", {"start": v(-23.87, 16) * mm, "end": v(-23.87, 0) * mm});
            skLineSegment(sketch, "E36.right", {"start": v(-7.82, 16) * mm, "end": v(-7.82, 0) * mm});
            skSolve(sketch);
        }
        {
            var Q0;
            {var subQ0=sQuery(id+"F51.wireOp",EDGE,"E36.right");Q0=makeQuery(id+"F51.imprint","IMPRINT",FACE,{"disambiguationData":[TD([[makeQuery(id+"F51.imprint","IMPRINT",EDGE,{"derivedFrom":subQ0}),1.0]])]});}
            var sketch = newSketch(context, id + "F52", { "sketchPlane" : qUnion([Q0])});
            skLineSegment(sketch, "E37.bottom", {"start": v(35.17, 15.57) * mm, "end": v(19.41, 15.57) * mm});
            skLineSegment(sketch, "E37.top", {"start": v(35.17, 0) * mm, "end": v(19.41, 0) * mm});
            skLineSegment(sketch, "E37.left", {"start": v(35.17, 15.57) * mm, "end": v(35.17, 0) * mm});
            skLineSegment(sketch, "E37.right", {"start": v(19.41, 15.57) * mm, "end": v(19.41, 0) * mm});
            skSolve(sketch);
        }
        {
            var Q0;
            Q0=makeQuery(id+"F51.imprint","IMPRINT",FACE,{"disambiguationData":[TD([[makeQuery(id+"F51.imprint","IMPRINT",EDGE,{"derivedFrom":sQuery(id+"F51.wireOp",EDGE,"E36.bottom")}),1.0]])]});
            extrude(context, id + "F53", {"entities" : qUnion([Q0]), "depth" : 16 * mm});
        }
        {
            var Q0;
            Q0=makeQuery(id+"F52.imprint","IMPRINT",FACE,{"disambiguationData":[TD([[makeQuery(id+"F52.imprint","IMPRINT",EDGE,{"derivedFrom":sQuery(id+"F52.wireOp",EDGE,"E37.bottom")}),1.0]])]});
            extrude(context, id + "F54", {"entities" : qUnion([Q0]), "operationType" : NewBodyOperationType.ADD, "depth" : 16 * mm});
        }
        {
            var Q0;
            Q0=makeQuery(id+"F53.opExtrude","CAP_EDGE",EDGE,{"disambiguationData":[OSD([sQuery(id+"F51.wireOp",EDGE,"E36.right")])],"isStart":false});
            chamfer(context, id + "F55", {"entities" : qUnion([Q0]), "width" : 15.24 * mm, "tangentPropagation" : true});
        }
        {
            var Q0;
            Q0=makeQuery(id+"F54.opExtrude","CAP_EDGE",EDGE,{"disambiguationData":[OSD([sQuery(id+"F52.wireOp",EDGE,"E37.right")])],"isStart":false});
            chamfer(context, id + "F56", {"entities" : qUnion([Q0]), "width" : 15.24 * mm, "tangentPropagation" : true});
        }
    });
